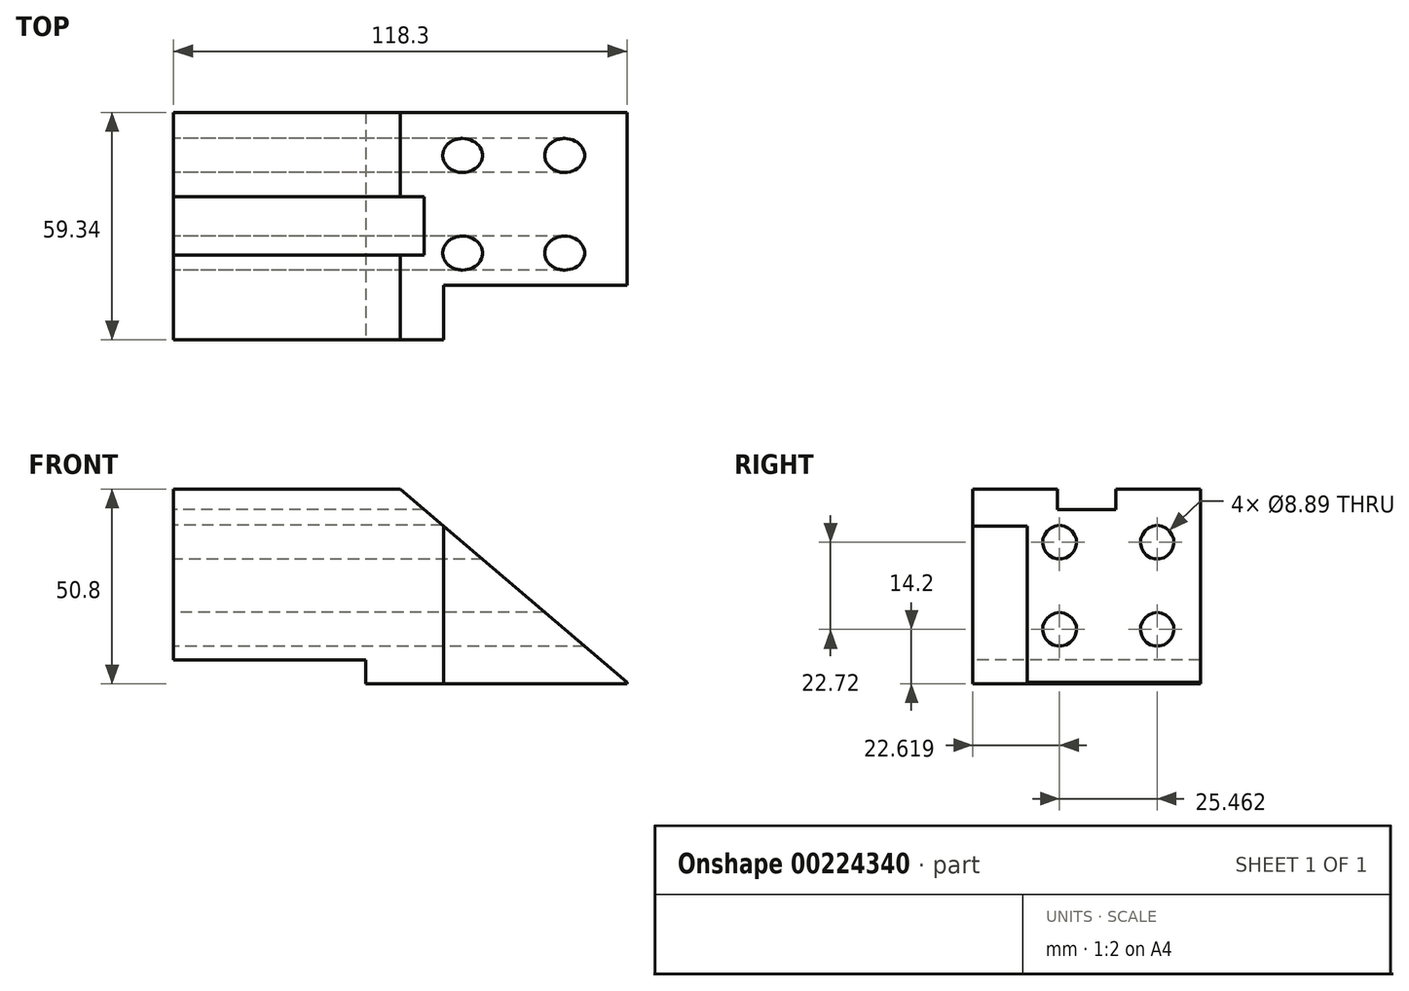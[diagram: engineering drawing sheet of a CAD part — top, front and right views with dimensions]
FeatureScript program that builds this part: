
annotation { "Feature Type Name" : "Feature", "Feature Type Description" : "" }
export const myFeature = defineFeature(function(context is Context, id is Id, definition is map)
    precondition{}
    {
        {
            var Q0;
            Q0=qCreatedBy(makeId("Top.planeOp"),FACE);
            var sketch = newSketch(context, id + "F0", { "sketchPlane" : qUnion([Q0])});
            skLineSegment(sketch, "E0.bottom", {"start": v(-59.15, 29.67) * mm, "end": v(59.15, 29.67) * mm});
            skLineSegment(sketch, "E0.top", {"start": v(-59.15, -29.67) * mm, "end": v(59.15, -29.67) * mm});
            skLineSegment(sketch, "E0.left", {"start": v(-59.15, 29.67) * mm, "end": v(-59.15, -29.67) * mm});
            skLineSegment(sketch, "E0.right", {"start": v(59.15, 29.67) * mm, "end": v(59.15, -29.67) * mm});
            skPoint(sketch, "E0.middle", {"position": v(0, 0) * mm});
            skSolve(sketch);
        }
        {
            var Q0;
            Q0 = qSketchRegion(id + "F0", true);
            extrude(context, id + "F1", {"entities" : qUnion([Q0]), "depth" : 50.8 * mm});
        }
        {
            var Q0;
            Q0=makeQuery(id+"F1.opExtrude","CAP_FACE",FACE,{"disambiguationData":[OSD([sQuery(id+"F0.wireOp",EDGE,"E0.bottom"),sQuery(id+"F0.wireOp",EDGE,"E0.top"),sQuery(id+"F0.wireOp",EDGE,"E0.left"),sQuery(id+"F0.wireOp",EDGE,"E0.right")])],"isStart":false});
            var sketch = newSketch(context, id + "F2", { "sketchPlane" : qUnion([Q0])});
            skLineSegment(sketch, "E1.bottom", {"start": v(11.35, -29.67) * mm, "end": v(63.85, -29.67) * mm});
            skLineSegment(sketch, "E1.top", {"start": v(11.35, -15.43) * mm, "end": v(63.85, -15.43) * mm});
            skLineSegment(sketch, "E1.left", {"start": v(11.35, -29.67) * mm, "end": v(11.35, -15.43) * mm});
            skLineSegment(sketch, "E1.right", {"start": v(63.85, -29.67) * mm, "end": v(63.85, -15.43) * mm});
            skSolve(sketch);
        }
        {
            var Q0;
            Q0 = qSketchRegion(id + "F2", true);
            extrude(context, id + "F3", {"entities" : qUnion([Q0]), "operationType" : NewBodyOperationType.REMOVE, "oppositeDirection" : true, "depth" : 112.01 * mm});
        }
        {
            var Q0;
            Q0=makeQuery(id+"F1.opExtrude","SWEPT_FACE",FACE,{"disambiguationData":[OSD([sQuery(id+"F0.wireOp",EDGE,"E0.top")])]});
            var sketch = newSketch(context, id + "F4", { "sketchPlane" : qUnion([Q0])});
            skLineSegment(sketch, "E2.bottom", {"start": v(-9, 0) * mm, "end": v(-59.15, 0) * mm});
            skLineSegment(sketch, "E2.top", {"start": v(-9, 6.17) * mm, "end": v(-59.15, 6.17) * mm});
            skLineSegment(sketch, "E2.left", {"start": v(-9, 0) * mm, "end": v(-9, 6.17) * mm});
            skLineSegment(sketch, "E2.right", {"start": v(-59.15, 0) * mm, "end": v(-59.15, 6.17) * mm});
            skSolve(sketch);
        }
        {
            var Q0;
            Q0=makeQuery(id+"F4.imprint","IMPRINT",FACE,{"disambiguationData":[TD([[makeQuery(id+"F4.imprint","IMPRINT",EDGE,{"derivedFrom":sQuery(id+"F4.wireOp",EDGE,"E2.bottom")}),1.0]])]});
            extrude(context, id + "F5", {"entities" : qUnion([Q0]), "operationType" : NewBodyOperationType.REMOVE, "oppositeDirection" : true, "depth" : 123.19 * mm});
        }
        {
            var Q0;
            Q0=makeQuery(id+"F1.opExtrude","SWEPT_FACE",FACE,{"disambiguationData":[OSD([sQuery(id+"F0.wireOp",EDGE,"E0.top")])]});
            var sketch = newSketch(context, id + "F6", { "sketchPlane" : qUnion([Q0])});
            skLineSegment(sketch, "E3", {"start": v(0, 50.8) * mm, "end": v(59.54, 0) * mm});
            skLineSegment(sketch, "E4", {"start": v(59.54, 0) * mm, "end": v(59.54, 50.8) * mm});
            skLineSegment(sketch, "E5", {"start": v(59.54, 50.8) * mm, "end": v(0, 50.8) * mm});
            skSolve(sketch);
        }
        {
            var Q0;
            {var subQ0=sQuery(id+"F6.wireOp",EDGE,"E5");var subQ1=sQuery(id+"F6.wireOp",EDGE,"E3");var subQ2=sQuery(id+"F0.wireOp",EDGE,"E0.top");var subQ3=makeQuery(id+"F6.imprint","INTERSECT",VERTEX,{"derivedFrom":[makeQuery(id+"F1.opExtrude","CAP_EDGE",EDGE,{"disambiguationData":[OSD([subQ2])],"isStart":false}),subQ1,subQ0]});Q0=makeQuery(id+"F6.imprint","IMPRINT",FACE,{"disambiguationData":[TD([[makeQuery(id+"F6.imprint","IMPRINT",EDGE,{"disambiguationData":[TD([[subQ3,-1.0]])],"derivedFrom":subQ1}),1.0]])]});}
            var Q1;
            {var subQ0=sQuery(id+"F6.wireOp",EDGE,"E4");Q1=makeQuery(id+"F6.imprint","IMPRINT",FACE,{"disambiguationData":[TD([[makeQuery(id+"F6.imprint","IMPRINT",EDGE,{"derivedFrom":subQ0}),1.0]])]});}
            extrude(context, id + "F7", {"entities" : qUnion([Q0, Q1]), "operationType" : NewBodyOperationType.REMOVE, "oppositeDirection" : true, "depth" : 96.52 * mm});
        }
        {
            var Q0;
            Q0=makeQuery(id+"F1.opExtrude","SWEPT_FACE",FACE,{"disambiguationData":[OSD([sQuery(id+"F0.wireOp",EDGE,"E0.left")])]});
            var sketch = newSketch(context, id + "F8", { "sketchPlane" : qUnion([Q0])});
            skLineSegment(sketch, "E6.bottom", {"start": v(7.64, 45.5) * mm, "end": v(-7.64, 45.5) * mm});
            skLineSegment(sketch, "E6.top", {"start": v(7.64, 56.1) * mm, "end": v(-7.64, 56.1) * mm});
            skLineSegment(sketch, "E6.left", {"start": v(7.64, 45.5) * mm, "end": v(7.64, 56.1) * mm});
            skLineSegment(sketch, "E6.right", {"start": v(-7.64, 45.5) * mm, "end": v(-7.64, 56.1) * mm});
            skPoint(sketch, "E6.middle", {"position": v(0, 50.8) * mm});
            skSolve(sketch);
        }
        {
            var Q0;
            {var subQ0=sQuery(id+"F8.wireOp",EDGE,"E6.bottom");Q0=makeQuery(id+"F8.imprint","IMPRINT",FACE,{"disambiguationData":[TD([[makeQuery(id+"F8.imprint","IMPRINT",EDGE,{"derivedFrom":subQ0}),-1.0]])]});}
            extrude(context, id + "F9", {"entities" : qUnion([Q0]), "operationType" : NewBodyOperationType.REMOVE, "oppositeDirection" : true, "depth" : 203.96 * mm});
        }
        {
            var Q0;
            Q0=makeQuery(id+"F1.opExtrude","SWEPT_FACE",FACE,{"disambiguationData":[OSD([sQuery(id+"F0.wireOp",EDGE,"E0.left")])]});
            var sketch = newSketch(context, id + "F10", { "sketchPlane" : qUnion([Q0])});
            skCircle(sketch, "E7", {"center": v(7.05, 36.92) * mm, "radius": 4.45 * mm});
            skCircle(sketch, "E8", {"center": v(-18.41, 36.92) * mm, "radius": 4.45 * mm});
            skCircle(sketch, "E9", {"center": v(-18.41, 14.2) * mm, "radius": 4.45 * mm});
            skCircle(sketch, "E10", {"center": v(7.05, 14.2) * mm, "radius": 4.45 * mm});
            skSolve(sketch);
        }
        {
            var Q0;
            Q0=makeQuery(id+"F10.imprint","IMPRINT",FACE,{"disambiguationData":[TD([[makeQuery(id+"F10.imprint","IMPRINT",EDGE,{"derivedFrom":sQuery(id+"F10.wireOp",EDGE,"E8")}),1.0]])]});
            var Q1;
            Q1=makeQuery(id+"F10.imprint","IMPRINT",FACE,{"disambiguationData":[TD([[makeQuery(id+"F10.imprint","IMPRINT",EDGE,{"derivedFrom":sQuery(id+"F10.wireOp",EDGE,"E7")}),1.0]])]});
            var Q2;
            Q2=makeQuery(id+"F10.imprint","IMPRINT",FACE,{"disambiguationData":[TD([[makeQuery(id+"F10.imprint","IMPRINT",EDGE,{"derivedFrom":sQuery(id+"F10.wireOp",EDGE,"E10")}),1.0]])]});
            var Q3;
            Q3=makeQuery(id+"F10.imprint","IMPRINT",FACE,{"disambiguationData":[TD([[makeQuery(id+"F10.imprint","IMPRINT",EDGE,{"derivedFrom":sQuery(id+"F10.wireOp",EDGE,"E9")}),1.0]])]});
            extrude(context, id + "F11", {"entities" : qUnion([Q0, Q1, Q2, Q3]), "operationType" : NewBodyOperationType.REMOVE, "oppositeDirection" : true, "depth" : 210.57 * mm});
        }
    });
